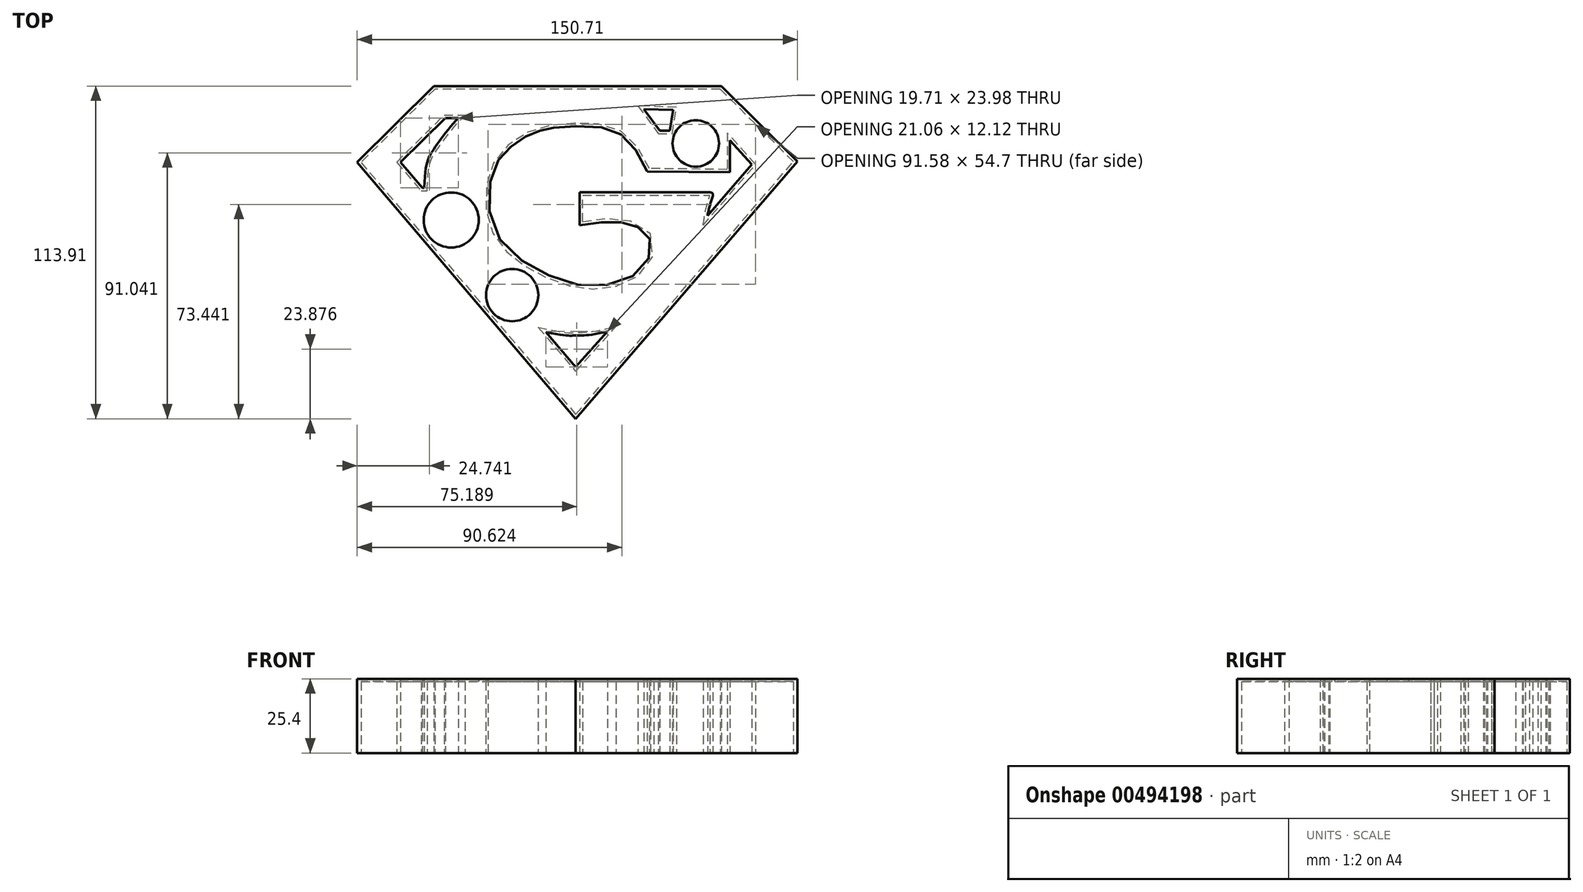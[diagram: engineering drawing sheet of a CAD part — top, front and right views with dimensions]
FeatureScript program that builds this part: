
annotation { "Feature Type Name" : "Feature", "Feature Type Description" : "" }
export const myFeature = defineFeature(function(context is Context, id is Id, definition is map)
    precondition{}
    {
        {
            var Q0;
            Q0=qCreatedBy(makeId("Top.planeOp"),FACE);
            var sketch = newSketch(context, id + "F0", { "sketchPlane" : qUnion([Q0])});
            skLineSegment(sketch, "E0", {"start": v(-74.83, 17.46) * mm, "end": v(0, -70.4) * mm});
            skLineSegment(sketch, "E1", {"start": v(0, -70.4) * mm, "end": v(75.88, 17.75) * mm});
            skLineSegment(sketch, "E2", {"start": v(75.88, 17.75) * mm, "end": v(49.86, 43.52) * mm});
            skLineSegment(sketch, "E3", {"start": v(49.86, 43.52) * mm, "end": v(-48.56, 43.52) * mm});
            skLineSegment(sketch, "E4", {"start": v(-48.56, 43.52) * mm, "end": v(-74.83, 17.46) * mm});
            skLineSegment(sketch, "E5", {"start": v(-59.94, 17.46) * mm, "end": v(-44.64, 32.64) * mm});
            skLineSegment(sketch, "E6", {"start": v(-44.64, 32.64) * mm, "end": v(-40.24, 32.64) * mm});
            skLineSegment(sketch, "E7", {"start": v(-59.94, 17.46) * mm, "end": v(-52.45, 8.66) * mm});
            skLineSegment(sketch, "E8", {"start": v(-52.45, 8.66) * mm, "end": v(-51.82, 8.66) * mm});
            skFitSpline(sketch, "E9", {"points": [v(-51.82, 8.66) * mm, v(-49.01, 21.3) * mm, v(-40.24, 32.64) * mm], "startDerivative": vector(2.11, 50.89) * mm, "endDerivative": vector(20.03, 21.12) * mm});
            skFitSpline(sketch, "E10", {"points": [v(24.51, 14.3) * mm, v(17.32, 25.5) * mm, v(8.15, 29.46) * mm, v(-6.49, 29.38) * mm, v(-11.6, 28.42) * mm, v(-17, 26.34) * mm, v(-23.1, 22.05) * mm, v(-28.35, 14.3) * mm, v(-27.93, -5.35) * mm, v(-11.88, -20.02) * mm, v(8.46, -24.86) * mm, v(23.68, -17.8) * mm, v(25.2, -8.53) * mm, v(20.08, -4.24) * mm, v(12.33, -2.86) * mm, v(1.4, -4.1) * mm], "startDerivative": vector(-78.23, 181.81) * mm, "endDerivative": vector(-173.23, -28.5) * mm});
            skLineSegment(sketch, "E11", {"start": v(1.4, -4.1) * mm, "end": v(1.4, 7.14) * mm});
            skLineSegment(sketch, "E12", {"start": v(1.4, 7.14) * mm, "end": v(46, 7.14) * mm});
            skLineSegment(sketch, "E13", {"start": v(45.15, -0.78) * mm, "end": v(60.25, 16.73) * mm});
            skLineSegment(sketch, "E14", {"start": v(60.25, 16.73) * mm, "end": v(52.84, 24.93) * mm});
            skLineSegment(sketch, "E15", {"start": v(52.84, 24.93) * mm, "end": v(52.84, 13.98) * mm});
            skLineSegment(sketch, "E16", {"start": v(52.84, 13.98) * mm, "end": v(24.51, 14.3) * mm});
            skFitSpline(sketch, "E17", {"points": [v(45.15, -0.78) * mm, v(46.58, 4.8) * mm, v(46, 7.14) * mm], "startDerivative": vector(1.7, 10.85) * mm, "endDerivative": vector(-10.2, 0) * mm});
            skLineSegment(sketch, "E18", {"start": v(-10.17, -40.64) * mm, "end": v(0, -52.58) * mm});
            skLineSegment(sketch, "E19", {"start": v(0, -52.58) * mm, "end": v(10.89, -40.45) * mm});
            skFitSpline(sketch, "E20", {"points": [v(-10.17, -40.64) * mm, v(0, -41.84) * mm, v(10.89, -40.45) * mm], "startDerivative": vector(46.45, -9.9) * mm, "endDerivative": vector(37.05, 9.51) * mm});
            skLineSegment(sketch, "E21", {"start": v(23.33, 35.69) * mm, "end": v(28.75, 28.3) * mm});
            skLineSegment(sketch, "E22", {"start": v(28.75, 28.3) * mm, "end": v(32.2, 28.3) * mm});
            skLineSegment(sketch, "E23", {"start": v(32.2, 28.3) * mm, "end": v(33.31, 35.32) * mm});
            skLineSegment(sketch, "E24", {"start": v(33.31, 35.32) * mm, "end": v(23.33, 35.69) * mm});
            skCircle(sketch, "E25", {"center": v(-42.63, -2.3) * mm, "radius": 8.42 * mm});
            skCircle(sketch, "E26", {"center": v(-21.76, -28.03) * mm, "radius": 7.95 * mm});
            skCircle(sketch, "E27", {"center": v(41.1, 23.9) * mm, "radius": 6.95 * mm});
            skSolve(sketch);
        }
        {
            var Q0;
            Q0 = qSketchRegion(id + "F0", true);
            extrude(context, id + "F1", {"entities" : qUnion([Q0]), "depth" : 25.4 * mm});
        }
        {
            var Q0;
            Q0=makeQuery(id+"F1.opExtrude","CAP_FACE",FACE,{"disambiguationData":[OSD([sQuery(id+"F0.wireOp",EDGE,"E0"),sQuery(id+"F0.wireOp",EDGE,"E1"),sQuery(id+"F0.wireOp",EDGE,"E2"),sQuery(id+"F0.wireOp",EDGE,"E3"),sQuery(id+"F0.wireOp",EDGE,"E4"),sQuery(id+"F0.wireOp",EDGE,"E5"),sQuery(id+"F0.wireOp",EDGE,"E6"),sQuery(id+"F0.wireOp",EDGE,"E7"),sQuery(id+"F0.wireOp",EDGE,"E8"),sQuery(id+"F0.wireOp",EDGE,"E9"),sQuery(id+"F0.wireOp",EDGE,"E10"),sQuery(id+"F0.wireOp",EDGE,"E11"),sQuery(id+"F0.wireOp",EDGE,"E12"),sQuery(id+"F0.wireOp",EDGE,"E13"),sQuery(id+"F0.wireOp",EDGE,"E14"),sQuery(id+"F0.wireOp",EDGE,"E15"),sQuery(id+"F0.wireOp",EDGE,"E16"),sQuery(id+"F0.wireOp",EDGE,"E17"),sQuery(id+"F0.wireOp",EDGE,"E18"),sQuery(id+"F0.wireOp",EDGE,"E19"),sQuery(id+"F0.wireOp",EDGE,"E20"),sQuery(id+"F0.wireOp",EDGE,"E21"),sQuery(id+"F0.wireOp",EDGE,"E22"),sQuery(id+"F0.wireOp",EDGE,"E23"),sQuery(id+"F0.wireOp",EDGE,"E24")])],"isStart":true});
            shell(context, id + "F2", {"entities" : qUnion([Q0]), "thickness" : 1 * mm});
        }
        {
            var Q0;
            {var subQ0=sQuery(id+"F0.wireOp",EDGE,"E27");var subQ1=sQuery(id+"F0.wireOp",EDGE,"E26");var subQ2=sQuery(id+"F0.wireOp",EDGE,"E25");var subQ3=sQuery(id+"F0.wireOp",EDGE,"E24");var subQ4=sQuery(id+"F0.wireOp",EDGE,"E23");var subQ5=sQuery(id+"F0.wireOp",EDGE,"E22");var subQ6=sQuery(id+"F0.wireOp",EDGE,"E21");var subQ7=sQuery(id+"F0.wireOp",EDGE,"E20");var subQ8=sQuery(id+"F0.wireOp",EDGE,"E19");var subQ9=sQuery(id+"F0.wireOp",EDGE,"E18");var subQ10=sQuery(id+"F0.wireOp",EDGE,"E17");var subQ11=sQuery(id+"F0.wireOp",EDGE,"E16");var subQ12=sQuery(id+"F0.wireOp",EDGE,"E15");var subQ13=sQuery(id+"F0.wireOp",EDGE,"E14");var subQ14=sQuery(id+"F0.wireOp",EDGE,"E13");var subQ15=sQuery(id+"F0.wireOp",EDGE,"E12");var subQ16=sQuery(id+"F0.wireOp",EDGE,"E11");var subQ17=sQuery(id+"F0.wireOp",EDGE,"E10");var subQ18=sQuery(id+"F0.wireOp",EDGE,"E9");var subQ19=sQuery(id+"F0.wireOp",EDGE,"E8");var subQ20=sQuery(id+"F0.wireOp",EDGE,"E7");var subQ21=sQuery(id+"F0.wireOp",EDGE,"E6");var subQ22=sQuery(id+"F0.wireOp",EDGE,"E5");var subQ23=sQuery(id+"F0.wireOp",EDGE,"E4");var subQ24=sQuery(id+"F0.wireOp",EDGE,"E3");var subQ25=sQuery(id+"F0.wireOp",EDGE,"E2");var subQ26=sQuery(id+"F0.wireOp",EDGE,"E1");var subQ27=sQuery(id+"F0.wireOp",EDGE,"E0");Q0=makeQuery(id+"F2.opShell","OFFSET_FACE",FACE,{"disambiguationData":[OSD([subQ27,subQ26,subQ25,subQ24,subQ23,subQ22,subQ21,subQ20,subQ19,subQ18,subQ17,subQ16,subQ15,subQ14,subQ13,subQ12,subQ11,subQ10,subQ9,subQ8,subQ7,subQ6,subQ5,subQ4,subQ3,subQ2,subQ1,subQ0]),TDD([makeQuery(id+"F1.opExtrude","CAP_FACE",FACE,{"disambiguationData":[OSD([subQ27,subQ26,subQ25,subQ24,subQ23,subQ22,subQ21,subQ20,subQ19,subQ18,subQ17,subQ16,subQ15,subQ14,subQ13,subQ12,subQ11,subQ10,subQ9,subQ8,subQ7,subQ6,subQ5,subQ4,subQ3,subQ2,subQ1,subQ0])],"isStart":true})]),OD(4.0)]});}
            var Q1;
            {var subQ0=sQuery(id+"F0.wireOp",EDGE,"E27");var subQ1=sQuery(id+"F0.wireOp",EDGE,"E26");var subQ2=sQuery(id+"F0.wireOp",EDGE,"E25");var subQ3=sQuery(id+"F0.wireOp",EDGE,"E24");var subQ4=sQuery(id+"F0.wireOp",EDGE,"E23");var subQ5=sQuery(id+"F0.wireOp",EDGE,"E22");var subQ6=sQuery(id+"F0.wireOp",EDGE,"E21");var subQ7=sQuery(id+"F0.wireOp",EDGE,"E20");var subQ8=sQuery(id+"F0.wireOp",EDGE,"E19");var subQ9=sQuery(id+"F0.wireOp",EDGE,"E18");var subQ10=sQuery(id+"F0.wireOp",EDGE,"E17");var subQ11=sQuery(id+"F0.wireOp",EDGE,"E16");var subQ12=sQuery(id+"F0.wireOp",EDGE,"E15");var subQ13=sQuery(id+"F0.wireOp",EDGE,"E14");var subQ14=sQuery(id+"F0.wireOp",EDGE,"E13");var subQ15=sQuery(id+"F0.wireOp",EDGE,"E12");var subQ16=sQuery(id+"F0.wireOp",EDGE,"E11");var subQ17=sQuery(id+"F0.wireOp",EDGE,"E10");var subQ18=sQuery(id+"F0.wireOp",EDGE,"E9");var subQ19=sQuery(id+"F0.wireOp",EDGE,"E8");var subQ20=sQuery(id+"F0.wireOp",EDGE,"E7");var subQ21=sQuery(id+"F0.wireOp",EDGE,"E6");var subQ22=sQuery(id+"F0.wireOp",EDGE,"E5");var subQ23=sQuery(id+"F0.wireOp",EDGE,"E4");var subQ24=sQuery(id+"F0.wireOp",EDGE,"E3");var subQ25=sQuery(id+"F0.wireOp",EDGE,"E2");var subQ26=sQuery(id+"F0.wireOp",EDGE,"E1");var subQ27=sQuery(id+"F0.wireOp",EDGE,"E0");Q1=makeQuery(id+"F2.opShell","OFFSET_FACE",FACE,{"disambiguationData":[OSD([subQ27,subQ26,subQ25,subQ24,subQ23,subQ22,subQ21,subQ20,subQ19,subQ18,subQ17,subQ16,subQ15,subQ14,subQ13,subQ12,subQ11,subQ10,subQ9,subQ8,subQ7,subQ6,subQ5,subQ4,subQ3,subQ2,subQ1,subQ0]),TDD([makeQuery(id+"F1.opExtrude","CAP_FACE",FACE,{"disambiguationData":[OSD([subQ27,subQ26,subQ25,subQ24,subQ23,subQ22,subQ21,subQ20,subQ19,subQ18,subQ17,subQ16,subQ15,subQ14,subQ13,subQ12,subQ11,subQ10,subQ9,subQ8,subQ7,subQ6,subQ5,subQ4,subQ3,subQ2,subQ1,subQ0])],"isStart":true})]),OD(5.0)]});}
            var Q2;
            {var subQ0=sQuery(id+"F0.wireOp",EDGE,"E27");var subQ1=sQuery(id+"F0.wireOp",EDGE,"E26");var subQ2=sQuery(id+"F0.wireOp",EDGE,"E25");var subQ3=sQuery(id+"F0.wireOp",EDGE,"E24");var subQ4=sQuery(id+"F0.wireOp",EDGE,"E23");var subQ5=sQuery(id+"F0.wireOp",EDGE,"E22");var subQ6=sQuery(id+"F0.wireOp",EDGE,"E21");var subQ7=sQuery(id+"F0.wireOp",EDGE,"E20");var subQ8=sQuery(id+"F0.wireOp",EDGE,"E19");var subQ9=sQuery(id+"F0.wireOp",EDGE,"E18");var subQ10=sQuery(id+"F0.wireOp",EDGE,"E17");var subQ11=sQuery(id+"F0.wireOp",EDGE,"E16");var subQ12=sQuery(id+"F0.wireOp",EDGE,"E15");var subQ13=sQuery(id+"F0.wireOp",EDGE,"E14");var subQ14=sQuery(id+"F0.wireOp",EDGE,"E13");var subQ15=sQuery(id+"F0.wireOp",EDGE,"E12");var subQ16=sQuery(id+"F0.wireOp",EDGE,"E11");var subQ17=sQuery(id+"F0.wireOp",EDGE,"E10");var subQ18=sQuery(id+"F0.wireOp",EDGE,"E9");var subQ19=sQuery(id+"F0.wireOp",EDGE,"E8");var subQ20=sQuery(id+"F0.wireOp",EDGE,"E7");var subQ21=sQuery(id+"F0.wireOp",EDGE,"E6");var subQ22=sQuery(id+"F0.wireOp",EDGE,"E5");var subQ23=sQuery(id+"F0.wireOp",EDGE,"E4");var subQ24=sQuery(id+"F0.wireOp",EDGE,"E3");var subQ25=sQuery(id+"F0.wireOp",EDGE,"E2");var subQ26=sQuery(id+"F0.wireOp",EDGE,"E1");var subQ27=sQuery(id+"F0.wireOp",EDGE,"E0");Q2=makeQuery(id+"F2.opShell","OFFSET_FACE",FACE,{"disambiguationData":[OSD([subQ27,subQ26,subQ25,subQ24,subQ23,subQ22,subQ21,subQ20,subQ19,subQ18,subQ17,subQ16,subQ15,subQ14,subQ13,subQ12,subQ11,subQ10,subQ9,subQ8,subQ7,subQ6,subQ5,subQ4,subQ3,subQ2,subQ1,subQ0]),TDD([makeQuery(id+"F1.opExtrude","CAP_FACE",FACE,{"disambiguationData":[OSD([subQ27,subQ26,subQ25,subQ24,subQ23,subQ22,subQ21,subQ20,subQ19,subQ18,subQ17,subQ16,subQ15,subQ14,subQ13,subQ12,subQ11,subQ10,subQ9,subQ8,subQ7,subQ6,subQ5,subQ4,subQ3,subQ2,subQ1,subQ0])],"isStart":true})]),OD(6.0)]});}
            extrude(context, id + "F3", {"entities" : qUnion([Q0, Q1, Q2]), "operationType" : NewBodyOperationType.REMOVE, "oppositeDirection" : true, "depth" : 105.3 * mm});
        }
    });
